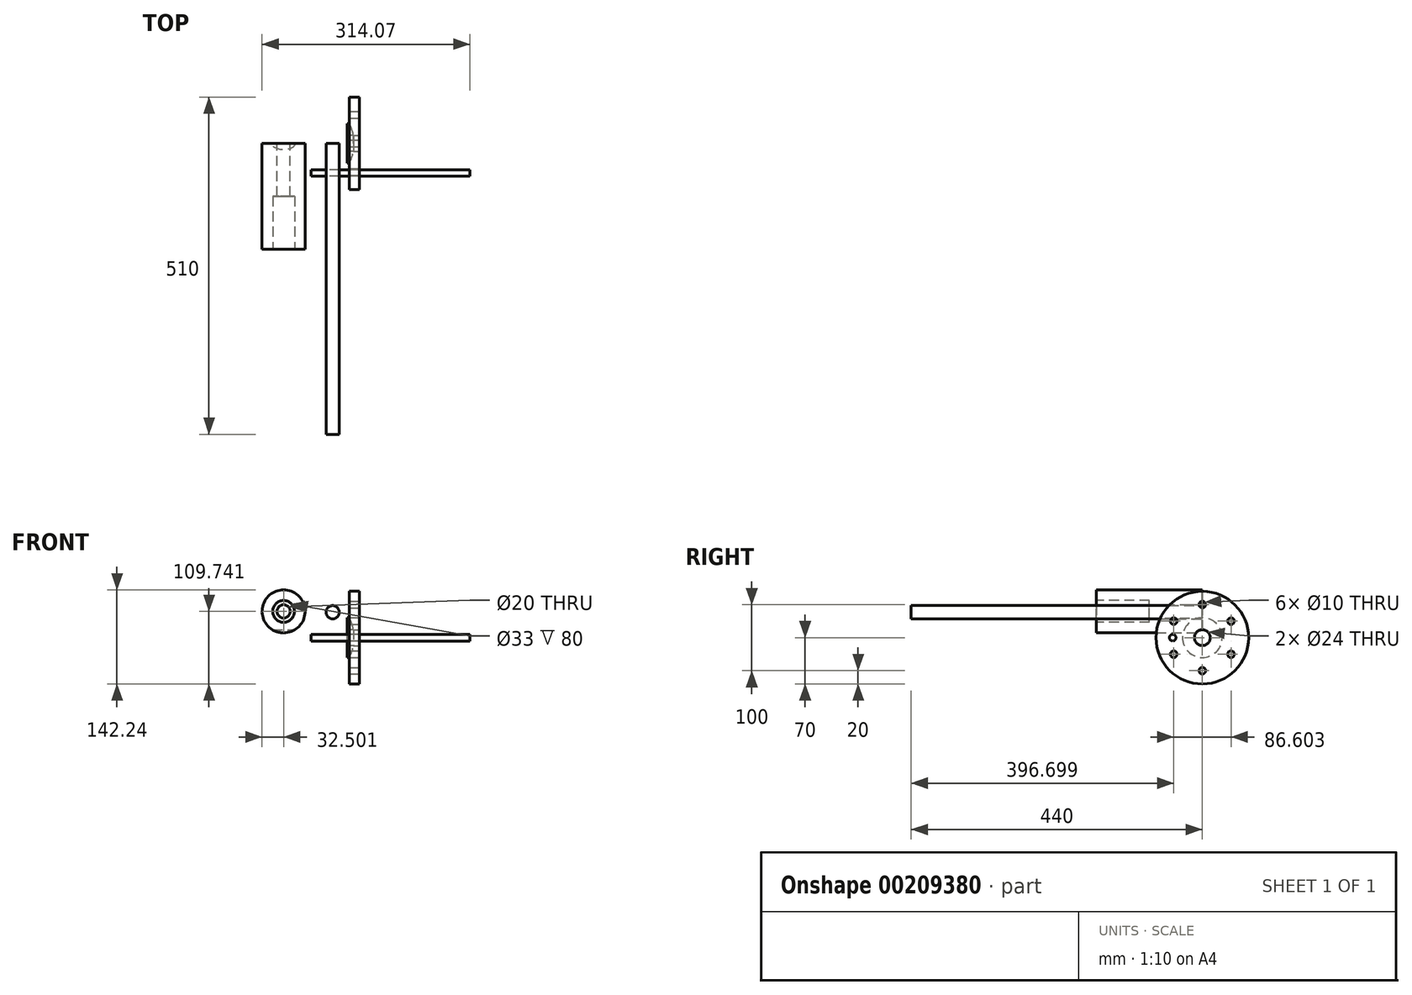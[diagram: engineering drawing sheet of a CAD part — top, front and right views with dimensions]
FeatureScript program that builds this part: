
annotation { "Feature Type Name" : "Feature", "Feature Type Description" : "" }
export const myFeature = defineFeature(function(context is Context, id is Id, definition is map)
    precondition{}
    {
        {
            var Q0;
            Q0=qCreatedBy(makeId("Top.planeOp"),FACE);
            var sketch = newSketch(context, id + "F0", { "sketchPlane" : qUnion([Q0])});
            skArc(sketch, "E0", {"start": v(57.66, -30) * mm, "mid": v(63.14, -15.44) * mm, "end": v(65, 0) * mm});
            skLineSegment(sketch, "E1", {"start": v(0, 0) * mm, "end": v(57.66, 0) * mm});
            skLineSegment(sketch, "E2.MirrorCS", {"start": v(57.66, -30) * mm, "end": v(57.66, 0) * mm});
            skLineSegment(sketch, "E3.MirrorCS", {"start": v(127.77, 0) * mm, "end": v(63.88, 0) * mm});
            skLineSegment(sketch, "E4.MirrorCS", {"start": v(63.88, -12) * mm, "end": v(63.88, 0) * mm});
            skLineSegment(sketch, "E5.trimOffspring", {"start": v(63.88, 0) * mm, "end": v(65, 0) * mm});
            skPoint(sketch, "E6.orphan", {"position": v(62.77, 0) * mm});
            skLineSegment(sketch, "E7", {"start": v(57.66, 30) * mm, "end": v(54.66, 30) * mm});
            skLineSegment(sketch, "E8", {"start": v(54.66, 30) * mm, "end": v(54.66, 12) * mm});
            skLineSegment(sketch, "E9", {"start": v(54.66, -30) * mm, "end": v(57.66, -30) * mm});
            skArc(sketch, "E10", {"start": v(65, 0) * mm, "mid": v(63.14, -15.44) * mm, "end": v(57.66, -30) * mm});
            skArc(sketch, "E11", {"start": v(57.66, 30) * mm, "mid": v(61.44, 21.23) * mm, "end": v(63.88, 12) * mm});
            skLineSegment(sketch, "E12", {"start": v(63.88, 12) * mm, "end": v(54.66, 12) * mm});
            skPoint(sketch, "E13.orphan", {"position": v(57.66, 0) * mm});
            skPoint(sketch, "E14.end.orphan", {"position": v(63.88, 0) * mm});
            skArc(sketch, "E15.trimOffspring", {"start": v(63.88, 12) * mm, "mid": v(61.44, 21.23) * mm, "end": v(57.66, 30) * mm});
            skSolve(sketch);
        }
        {
            var Q0;
            Q0=makeQuery(id+"F0.imprint","IMPRINT",FACE,{"disambiguationData":[TD([[makeQuery(id+"F0.imprint","IMPRINT",EDGE,{"derivedFrom":sQuery(id+"F0.wireOp",EDGE,"E7")}),1.0]])]});
            var Q1;
            Q1=sQuery(id+"F0.wireOp",EDGE,"E1");
            revolve(context, id + "F1", {"entities" : qUnion([Q0]), "axis" : qUnion([Q1]), "revolveType" : RevolveType.FULL});
        }
        {
            var Q0;
            Q0=qCreatedBy(makeId("Front.planeOp"),FACE);
            var sketch = newSketch(context, id + "F2", { "sketchPlane" : qUnion([Q0])});
            skCircle(sketch, "E16", {"center": v(-41.57, 39.74) * mm, "radius": 10 * mm});
            skCircle(sketch, "E17", {"center": v(-41.57, 39.74) * mm, "radius": 32.5 * mm});
            skSolve(sketch);
        }
        {
            var Q0;
            Q0 = qSketchRegion(id + "F2", true);
            extrude(context, id + "F3", {"entities" : qUnion([Q0]), "depth" : 160 * mm});
        }
        {
            var Q0;
            Q0=makeQuery(id+"F3.opExtrude","CAP_FACE",FACE,{"disambiguationData":[OSD([sQuery(id+"F2.wireOp",EDGE,"E16"),sQuery(id+"F2.wireOp",EDGE,"E17")])],"isStart":false});
            var sketch = newSketch(context, id + "F4", { "sketchPlane" : qUnion([Q0])});
            skCircle(sketch, "E18.0", {"center": v(-41.57, 39.74) * mm, "radius": 10 * mm});
            skCircle(sketch, "E19", {"center": v(-41.57, 39.74) * mm, "radius": 16.5 * mm});
            skSolve(sketch);
        }
        {
            var Q0;
            Q0=makeQuery(id+"F4.imprint","IMPRINT",FACE,{"disambiguationData":[TD([[makeQuery(id+"F4.imprint","IMPRINT",EDGE,{"derivedFrom":sQuery(id+"F4.wireOp",EDGE,"E18.0")}),-1.0]])]});
            extrude(context, id + "F5", {"entities" : qUnion([Q0]), "operationType" : NewBodyOperationType.REMOVE, "oppositeDirection" : true, "depth" : 80 * mm});
        }
        {
            var Q0;
            Q0=qCreatedBy(makeId("Front.planeOp"),FACE);
            var sketch = newSketch(context, id + "F6", { "sketchPlane" : qUnion([Q0])});
            skCircle(sketch, "E20", {"center": v(32.6, 38.45) * mm, "radius": 10 * mm});
            skSolve(sketch);
        }
        {
            var Q0;
            Q0=makeQuery(id+"F6.imprint","IMPRINT",FACE,{"disambiguationData":[TD([[makeQuery(id+"F6.imprint","IMPRINT",EDGE,{"derivedFrom":sQuery(id+"F6.wireOp",EDGE,"E20")}),1.0]])]});
            extrude(context, id + "F7", {"entities" : qUnion([Q0]), "depth" : 440 * mm});
        }
        {
            var Q0;
            Q0=qCreatedBy(makeId("Top.planeOp"),FACE);
            var sketch = newSketch(context, id + "F8", { "sketchPlane" : qUnion([Q0])});
            skArc(sketch, "E21.0", {"start": v(65, 0) * mm, "mid": v(63.14, -15.44) * mm, "end": v(57.66, -30) * mm});
            skLineSegment(sketch, "E22", {"start": v(57.66, -30) * mm, "end": v(57.66, -70) * mm});
            skLineSegment(sketch, "E23", {"start": v(57.66, -70) * mm, "end": v(72.66, -70) * mm});
            skLineSegment(sketch, "E24", {"start": v(72.66, -70) * mm, "end": v(72.66, 0) * mm});
            skLineSegment(sketch, "E25", {"start": v(65, 0) * mm, "end": v(72.66, 0) * mm});
            skSolve(sketch);
        }
        {
            var Q0;
            Q0 = qSketchRegion(id + "F8", true);
            var Q1;
            Q1=sQuery(id+"F8.wireOp",EDGE,"E25");
            revolve(context, id + "F9", {"entities" : qUnion([Q0]), "axis" : qUnion([Q1]), "revolveType" : RevolveType.FULL});
        }
        {
            var Q0;
            Q0=makeQuery(id+"F9.opRevolve","SWEPT_FACE",FACE,{"disambiguationData":[OSD([sQuery(id+"F8.wireOp",EDGE,"E24")])]});
            var sketch = newSketch(context, id + "F10", { "sketchPlane" : qUnion([Q0])});
            skPoint(sketch, "E26", {"position": v(0, 0) * mm});
            skCircle(sketch, "E27", {"center": v(0, 50) * mm, "radius": 5 * mm});
            skCircle(sketch, "E28.1.0", {"center": v(-43.3, 25) * mm, "radius": 5 * mm});
            skCircle(sketch, "E28.2.0", {"center": v(-43.3, -25) * mm, "radius": 5 * mm});
            skCircle(sketch, "E28.3.0", {"center": v(0, -50) * mm, "radius": 5 * mm});
            skCircle(sketch, "E28.4.0", {"center": v(43.3, -25) * mm, "radius": 5 * mm});
            skCircle(sketch, "E28.5.0", {"center": v(43.3, 25) * mm, "radius": 5 * mm});
            skSolve(sketch);
        }
        {
            var Q0;
            Q0=sQuery(id+"F10.wireOp",VERTEX,"E26");
            var Q1;
            Q1=makeQuery(id+"F3.opExtrude","SWEPT_BODY",BODY,{"disambiguationData":[OSD([sQuery(id+"F2.wireOp",EDGE,"E16"),sQuery(id+"F2.wireOp",EDGE,"E17")])]});
            var Q2;
            Q2=makeQuery(id+"F9.opRevolve","SWEPT_BODY",BODY,{"disambiguationData":[OSD([sQuery(id+"F8.wireOp",EDGE,"E21.0"),sQuery(id+"F8.wireOp",EDGE,"E22"),sQuery(id+"F8.wireOp",EDGE,"E23"),sQuery(id+"F8.wireOp",EDGE,"E24"),sQuery(id+"F8.wireOp",EDGE,"E25")])]});
            hole(context, id + "F11", {"style" : HoleStyle.SIMPLE, "endStyle" : HoleEndStyle.THROUGH, "holeDiameter" : 24 * mm, "locations" : qUnion([Q0]), "scope" : qUnion([Q1, Q2]), "isTappedThrough" : true});
        }
        {
            var Q0;
            Q0=sQuery(id+"F10.wireOp",VERTEX,"E27.center");
            var Q1;
            Q1=sQuery(id+"F10.wireOp",VERTEX,"E28.5.0.center");
            var Q2;
            Q2=sQuery(id+"F10.wireOp",VERTEX,"E28.4.0.center");
            var Q3;
            Q3=sQuery(id+"F10.wireOp",VERTEX,"E28.3.0.center");
            var Q4;
            Q4=sQuery(id+"F10.wireOp",VERTEX,"E28.2.0.center");
            var Q5;
            Q5=sQuery(id+"F10.wireOp",VERTEX,"E28.1.0.center");
            var Q6;
            Q6=makeQuery(id+"F9.opRevolve","SWEPT_BODY",BODY,{"disambiguationData":[OSD([sQuery(id+"F8.wireOp",EDGE,"E21.0"),sQuery(id+"F8.wireOp",EDGE,"E22"),sQuery(id+"F8.wireOp",EDGE,"E23"),sQuery(id+"F8.wireOp",EDGE,"E24"),sQuery(id+"F8.wireOp",EDGE,"E25")])]});
            hole(context, id + "F12", {"style" : HoleStyle.SIMPLE, "endStyle" : HoleEndStyle.THROUGH, "holeDiameter" : 10 * mm, "locations" : qUnion([Q0, Q1, Q2, Q3, Q4, Q5]), "scope" : qUnion([Q6]), "isTappedThrough" : true});
        }
        {
            var Q0;
            Q0=qCreatedBy(makeId("Right.planeOp"),FACE);
            var sketch = newSketch(context, id + "F13", { "sketchPlane" : qUnion([Q0])});
            skCircle(sketch, "E29", {"center": v(-44.83, 0) * mm, "radius": 5 * mm});
            skSolve(sketch);
        }
        {
            var Q0;
            Q0=makeQuery(id+"F13.imprint","IMPRINT",FACE,{"disambiguationData":[TD([[makeQuery(id+"F13.imprint","IMPRINT",EDGE,{"derivedFrom":sQuery(id+"F13.wireOp",EDGE,"E29")}),1.0]])]});
            extrude(context, id + "F14", {"entities" : qUnion([Q0]), "depth" : 240 * mm});
        }
        {
            var Q0;
            Q0=makeQuery(id+"F14.opExtrude","SWEPT_BODY",BODY,{"disambiguationData":[OSD([sQuery(id+"F13.wireOp",EDGE,"E29")])]});
            transform(context, id + "F15", {"entities" : qUnion([Q0]), "transformType" : TransformType.TRANSLATION_3D, "dx" : 0 * mm, "dy" : 0 * mm, "dz" : 0 * mm, "makeCopy" : true});
        }
    });
